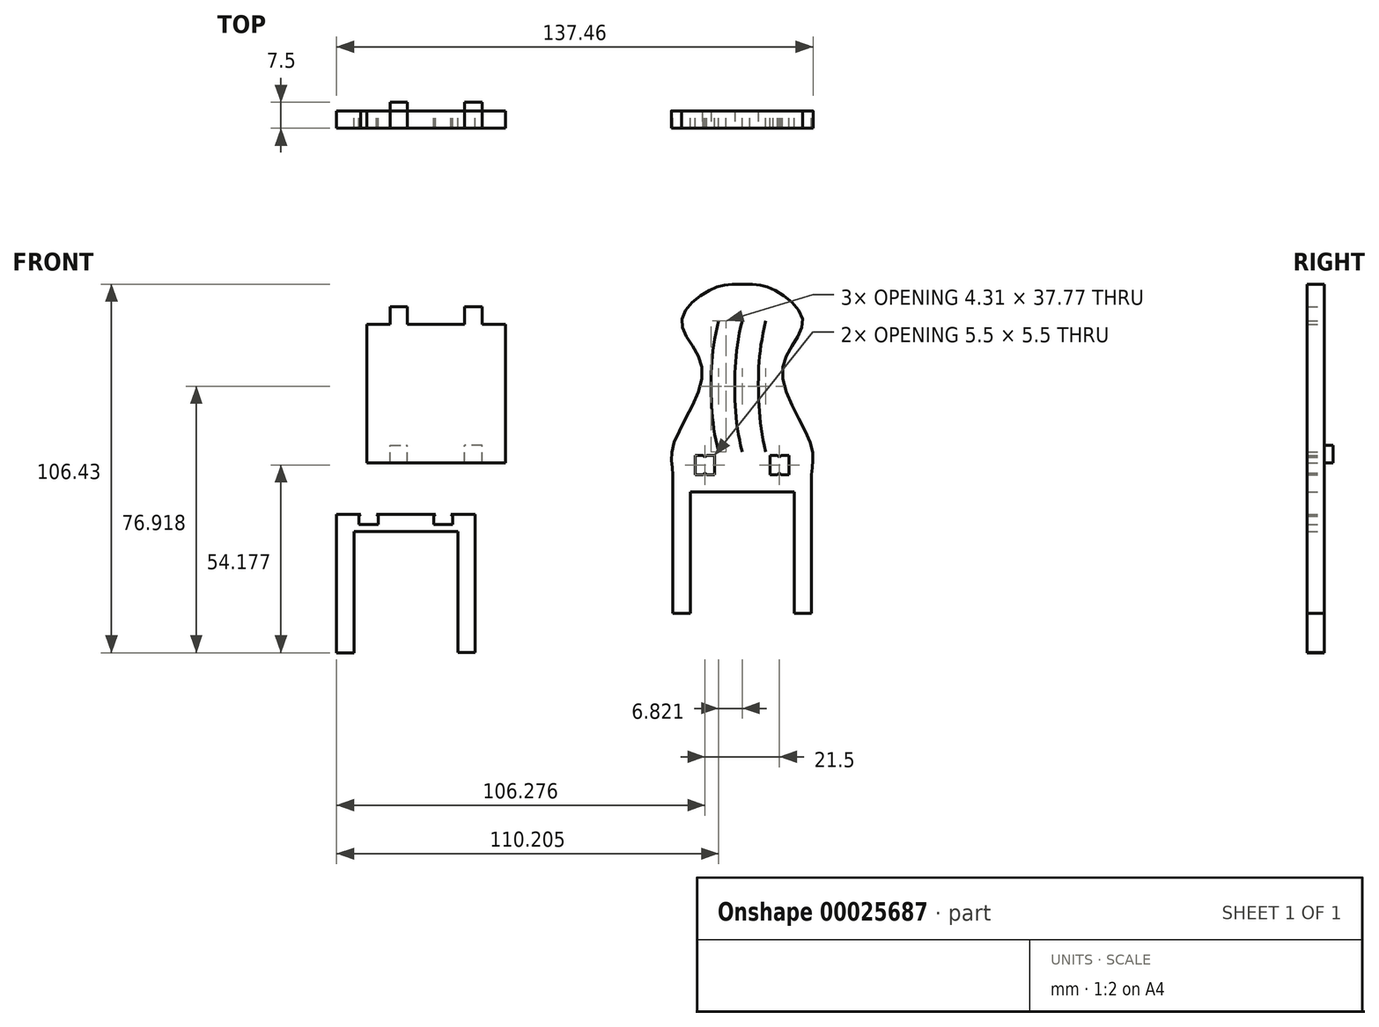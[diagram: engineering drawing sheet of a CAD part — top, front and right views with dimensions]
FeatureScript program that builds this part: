
annotation { "Feature Type Name" : "Feature", "Feature Type Description" : "" }
export const myFeature = defineFeature(function(context is Context, id is Id, definition is map)
    precondition{}
    {
        {
            var Q0;
            Q0=qCreatedBy(makeId("Front.planeOp"),FACE);
            var sketch = newSketch(context, id + "F0", { "sketchPlane" : qUnion([Q0])});
            skLineSegment(sketch, "E0.bottom", {"start": v(49.04, 57.77) * mm, "end": v(89.04, 57.77) * mm, "construction": true});
            skLineSegment(sketch, "E0.top", {"start": v(49.04, -37.23) * mm, "end": v(89.04, -37.23) * mm, "construction": true});
            skLineSegment(sketch, "E0.left", {"start": v(49.04, 57.77) * mm, "end": v(49.04, -37.23) * mm, "construction": true});
            skLineSegment(sketch, "E0.right", {"start": v(89.04, 57.77) * mm, "end": v(89.04, -37.23) * mm, "construction": true});
            skLineSegment(sketch, "E1", {"start": v(49.04, 2.77) * mm, "end": v(89.04, 2.77) * mm, "construction": true});
            skLineSegment(sketch, "E2", {"start": v(49.04, 2.77) * mm, "end": v(49.04, -37.23) * mm});
            skLineSegment(sketch, "E3", {"start": v(54.04, -37.23) * mm, "end": v(54.04, -2.23) * mm});
            skLineSegment(sketch, "E4", {"start": v(54.04, -2.23) * mm, "end": v(84.04, -2.23) * mm});
            skLineSegment(sketch, "E5", {"start": v(84.04, -2.23) * mm, "end": v(84.04, -37.23) * mm});
            skLineSegment(sketch, "E6", {"start": v(84.04, -37.23) * mm, "end": v(89.04, -37.23) * mm});
            skLineSegment(sketch, "E7", {"start": v(89.04, 2.77) * mm, "end": v(89.04, -37.23) * mm});
            skLineSegment(sketch, "E8", {"start": v(49.04, -37.23) * mm, "end": v(54.04, -37.23) * mm});
            skLineSegment(sketch, "E9", {"start": v(69.04, 57.77) * mm, "end": v(69.04, -0.66) * mm, "construction": true});
            skFitSpline(sketch, "E10", {"points": [v(49.04, 2.77) * mm, v(49.04, 10.95) * mm, v(57.45, 33.14) * mm, v(51.55, 46.97) * mm, v(59.84, 56.13) * mm, v(69.04, 57.77) * mm], "startDerivative": vector(0, 46.52) * mm, "endDerivative": vector(75.86, 0) * mm});
            skFitSpline(sketch, "E11.MirrorCS", {"points": [v(89.04, 2.77) * mm, v(89.04, 10.95) * mm, v(80.62, 33.14) * mm, v(86.52, 46.97) * mm, v(78.24, 56.13) * mm, v(69.04, 57.77) * mm], "startDerivative": vector(0, 46.52) * mm, "endDerivative": vector(-75.86, 0) * mm});
            skLineSegment(sketch, "E12", {"start": v(62.22, 47.14) * mm, "end": v(62.22, 9.37) * mm, "construction": true});
            skFitSpline(sketch, "E13", {"points": [v(62.22, 47.14) * mm, v(64.37, 28.26) * mm, v(62.22, 9.37) * mm], "startDerivative": vector(10.8, -41.93) * mm, "endDerivative": vector(-10.24, -39.43) * mm});
            skLineSegment(sketch, "E14", {"start": v(64.37, 28.26) * mm, "end": v(62.22, 28.26) * mm, "construction": true});
            skFitSpline(sketch, "E15.MirrorCS", {"points": [v(62.22, 47.14) * mm, v(60.06, 28.26) * mm, v(62.22, 9.37) * mm], "startDerivative": vector(-10.8, -41.93) * mm, "endDerivative": vector(10.24, -39.43) * mm});
            skFitSpline(sketch, "E16.MirrorCS", {"points": [v(75.86, 47.14) * mm, v(73.7, 28.26) * mm, v(75.86, 9.37) * mm], "startDerivative": vector(-10.8, -41.93) * mm, "endDerivative": vector(10.24, -39.43) * mm});
            skFitSpline(sketch, "E17.MirrorCS", {"points": [v(75.86, 47.14) * mm, v(78, 28.26) * mm, v(75.86, 9.37) * mm], "startDerivative": vector(10.8, -41.93) * mm, "endDerivative": vector(-10.24, -39.43) * mm});
            skFitSpline(sketch, "E18", {"points": [v(69.04, 47.14) * mm, v(71.19, 28.26) * mm, v(69.04, 9.37) * mm], "startDerivative": vector(10.8, -41.93) * mm, "endDerivative": vector(-10.24, -39.43) * mm});
            skLineSegment(sketch, "E19", {"start": v(69.04, 47.14) * mm, "end": v(69.04, 9.37) * mm, "construction": true});
            skFitSpline(sketch, "E20.MirrorCS", {"points": [v(69.04, 47.14) * mm, v(66.88, 28.26) * mm, v(69.04, 9.37) * mm], "startDerivative": vector(-10.8, -41.93) * mm, "endDerivative": vector(10.24, -39.43) * mm});
            skLineSegment(sketch, "E21", {"start": v(71.19, 28.26) * mm, "end": v(69.04, 28.26) * mm, "construction": true});
            skLineSegment(sketch, "E22.top", {"start": v(49.04, 8.27) * mm, "end": v(89.04, 8.27) * mm, "construction": true});
            skLineSegment(sketch, "E22.left", {"start": v(49.04, 2.77) * mm, "end": v(49.04, 8.27) * mm, "construction": true});
            skLineSegment(sketch, "E22.right", {"start": v(89.04, 2.77) * mm, "end": v(89.04, 8.27) * mm, "construction": true});
            skLineSegment(sketch, "E23.bottom", {"start": v(55.54, 8.27) * mm, "end": v(61.04, 8.27) * mm});
            skLineSegment(sketch, "E23.top", {"start": v(55.54, 2.77) * mm, "end": v(61.04, 2.77) * mm});
            skLineSegment(sketch, "E23.left", {"start": v(55.54, 8.27) * mm, "end": v(55.54, 2.77) * mm});
            skLineSegment(sketch, "E23.right", {"start": v(61.04, 8.27) * mm, "end": v(61.04, 2.77) * mm});
            skLineSegment(sketch, "E24", {"start": v(57.79, 8.27) * mm, "end": v(58.29, 7.77) * mm});
            skLineSegment(sketch, "E25", {"start": v(58.29, 7.77) * mm, "end": v(58.79, 8.27) * mm});
            skLineSegment(sketch, "E26", {"start": v(58.29, 7.77) * mm, "end": v(58.29, 8.27) * mm, "construction": true});
            skLineSegment(sketch, "E27", {"start": v(55.54, 5.52) * mm, "end": v(61.04, 5.52) * mm, "construction": true});
            skLineSegment(sketch, "E28.MirrorCS", {"start": v(57.79, 2.77) * mm, "end": v(58.29, 3.27) * mm});
            skLineSegment(sketch, "E29.MirrorCS", {"start": v(58.29, 3.27) * mm, "end": v(58.79, 2.77) * mm});
            skLineSegment(sketch, "E30.MirrorCS", {"start": v(79.79, 7.77) * mm, "end": v(79.79, 8.27) * mm});
            skLineSegment(sketch, "E31.MirrorCS", {"start": v(79.79, 7.77) * mm, "end": v(79.29, 8.27) * mm});
            skLineSegment(sketch, "E32.MirrorCS", {"start": v(80.29, 8.27) * mm, "end": v(79.79, 7.77) * mm});
            skLineSegment(sketch, "E33.MirrorCS", {"start": v(80.29, 2.77) * mm, "end": v(79.79, 3.27) * mm});
            skLineSegment(sketch, "E34.MirrorCS", {"start": v(79.79, 3.27) * mm, "end": v(79.29, 2.77) * mm});
            skLineSegment(sketch, "E35.MirrorCS", {"start": v(77.04, 8.27) * mm, "end": v(77.04, 2.77) * mm});
            skLineSegment(sketch, "E36.MirrorCS", {"start": v(82.54, 8.27) * mm, "end": v(77.04, 8.27) * mm});
            skLineSegment(sketch, "E37.MirrorCS", {"start": v(82.54, 5.52) * mm, "end": v(77.04, 5.52) * mm, "construction": true});
            skLineSegment(sketch, "E38.MirrorCS", {"start": v(82.54, 2.77) * mm, "end": v(77.04, 2.77) * mm});
            skLineSegment(sketch, "E39.MirrorCS", {"start": v(82.54, 8.27) * mm, "end": v(82.54, 2.77) * mm});
            skSolve(sketch);
        }
        {
            var Q0;
            Q0=makeQuery(id+"F0.imprint","IMPRINT",FACE,{"disambiguationData":[TD([[makeQuery(id+"F0.imprint","IMPRINT",EDGE,{"derivedFrom":sQuery(id+"F0.wireOp",EDGE,"E2")}),1.0]])]});
            var Q1;
            {var subQ1=sQuery(id+"F0.wireOp",EDGE,"E24");Q1=makeQuery(id+"F0.imprint","IMPRINT",FACE,{"disambiguationData":[TD([[makeQuery(id+"F0.imprint","IMPRINT",EDGE,{"derivedFrom":subQ1}),1.0]])]});}
            var Q2;
            {var subQ1=sQuery(id+"F0.wireOp",EDGE,"E28.MirrorCS");Q2=makeQuery(id+"F0.imprint","IMPRINT",FACE,{"disambiguationData":[TD([[makeQuery(id+"F0.imprint","IMPRINT",EDGE,{"derivedFrom":subQ1}),-1.0]])]});}
            var Q3;
            {var subQ2=sQuery(id+"F0.wireOp",EDGE,"E33.MirrorCS");Q3=makeQuery(id+"F0.imprint","IMPRINT",FACE,{"disambiguationData":[TD([[makeQuery(id+"F0.imprint","IMPRINT",EDGE,{"derivedFrom":subQ2}),1.0]])]});}
            var Q4;
            {var subQ2=sQuery(id+"F0.wireOp",EDGE,"E30.MirrorCS");Q4=makeQuery(id+"F0.imprint","IMPRINT",FACE,{"disambiguationData":[TD([[makeQuery(id+"F0.imprint","IMPRINT",EDGE,{"derivedFrom":subQ2}),1.0]])]});}
            var Q5;
            {var subQ2=sQuery(id+"F0.wireOp",EDGE,"E30.MirrorCS");Q5=makeQuery(id+"F0.imprint","IMPRINT",FACE,{"disambiguationData":[TD([[makeQuery(id+"F0.imprint","IMPRINT",EDGE,{"derivedFrom":subQ2}),-1.0]])]});}
            extrude(context, id + "F1", {"entities" : qUnion([Q0, Q1, Q2, Q3, Q4, Q5]), "depth" : 5 * mm});
        }
        {
            var Q0;
            Q0=qCreatedBy(makeId("Front.planeOp"),FACE);
            var sketch = newSketch(context, id + "F2", { "sketchPlane" : qUnion([Q0])});
            skLineSegment(sketch, "E40.bottom", {"start": v(-39.28, 46.22) * mm, "end": v(0.72, 46.22) * mm});
            skLineSegment(sketch, "E40.top", {"start": v(-39.28, 6.22) * mm, "end": v(0.72, 6.22) * mm});
            skLineSegment(sketch, "E40.left", {"start": v(-39.28, 46.22) * mm, "end": v(-39.28, 6.22) * mm});
            skLineSegment(sketch, "E40.right", {"start": v(0.72, 46.22) * mm, "end": v(0.72, 6.22) * mm});
            skLineSegment(sketch, "E41.bottom", {"start": v(-32.53, 46.22) * mm, "end": v(-27.53, 46.22) * mm});
            skLineSegment(sketch, "E41.top", {"start": v(-32.53, 51.22) * mm, "end": v(-27.53, 51.22) * mm});
            skLineSegment(sketch, "E41.left", {"start": v(-32.53, 46.22) * mm, "end": v(-32.53, 51.22) * mm});
            skLineSegment(sketch, "E41.right", {"start": v(-27.53, 46.22) * mm, "end": v(-27.53, 51.22) * mm});
            skLineSegment(sketch, "E42", {"start": v(-19.28, 46.22) * mm, "end": v(-19.28, 55.96) * mm, "construction": true});
            skLineSegment(sketch, "E43.MirrorCS", {"start": v(-6.03, 46.22) * mm, "end": v(-6.03, 51.22) * mm});
            skLineSegment(sketch, "E44.MirrorCS", {"start": v(-6.03, 51.22) * mm, "end": v(-11.03, 51.22) * mm});
            skLineSegment(sketch, "E45.MirrorCS", {"start": v(-6.03, 46.22) * mm, "end": v(-11.03, 46.22) * mm});
            skLineSegment(sketch, "E46.MirrorCS", {"start": v(0.72, 46.22) * mm, "end": v(-39.28, 46.22) * mm});
            skLineSegment(sketch, "E47.MirrorCS", {"start": v(-11.03, 46.22) * mm, "end": v(-11.03, 51.22) * mm});
            skSolve(sketch);
        }
        {
            var Q0;
            Q0=qSketchRegion(id+"F2",true);
            extrude(context, id + "F3", {"entities" : qUnion([Q0]), "depth" : 5 * mm});
        }
        {
            var Q0;
            Q0=qCreatedBy(makeId("Front.planeOp"),FACE);
            var sketch = newSketch(context, id + "F4", { "sketchPlane" : qUnion([Q0])});
            skLineSegment(sketch, "E48", {"start": v(-48, -8.66) * mm, "end": v(-48, -48.66) * mm});
            skLineSegment(sketch, "E49", {"start": v(-48, -48.66) * mm, "end": v(-43, -48.66) * mm});
            skLineSegment(sketch, "E50", {"start": v(-43, -48.66) * mm, "end": v(-43, -13.66) * mm});
            skLineSegment(sketch, "E51", {"start": v(-43, -13.66) * mm, "end": v(-13, -13.66) * mm});
            skLineSegment(sketch, "E52", {"start": v(-13, -13.66) * mm, "end": v(-13, -48.51) * mm});
            skLineSegment(sketch, "E53", {"start": v(-13, -48.51) * mm, "end": v(-8, -48.51) * mm});
            skLineSegment(sketch, "E54", {"start": v(-8, -48.51) * mm, "end": v(-8, -8.66) * mm});
            skLineSegment(sketch, "E55", {"start": v(-8, -8.66) * mm, "end": v(-48, -8.66) * mm});
            skSolve(sketch);
        }
        {
            var Q0;
            Q0=makeQuery(id+"F4.imprint","IMPRINT",FACE,{"disambiguationData":[TD([[makeQuery(id+"F4.imprint","IMPRINT",EDGE,{"derivedFrom":sQuery(id+"F4.wireOp",EDGE,"E48")}),1.0]])]});
            extrude(context, id + "F5", {"entities" : qUnion([Q0]), "depth" : 5 * mm});
        }
        {
            var Q0;
            Q0=makeQuery(id+"F3.opExtrude","CAP_FACE",FACE,{"disambiguationData":[OSD([sQuery(id+"F2.wireOp",EDGE,"E40.top"),sQuery(id+"F2.wireOp",EDGE,"E40.left"),sQuery(id+"F2.wireOp",EDGE,"E40.right"),sQuery(id+"F2.wireOp",EDGE,"E41.top"),sQuery(id+"F2.wireOp",EDGE,"E41.left"),sQuery(id+"F2.wireOp",EDGE,"E41.right"),sQuery(id+"F2.wireOp",EDGE,"E43.MirrorCS"),sQuery(id+"F2.wireOp",EDGE,"E44.MirrorCS"),sQuery(id+"F2.wireOp",EDGE,"E46.MirrorCS"),sQuery(id+"F2.wireOp",EDGE,"E47.MirrorCS")])],"isStart":true});
            var sketch = newSketch(context, id + "F6", { "sketchPlane" : qUnion([Q0])});
            skLineSegment(sketch, "E56.bottom", {"start": v(32.53, 6.22) * mm, "end": v(27.53, 6.22) * mm});
            skLineSegment(sketch, "E56.top", {"start": v(32.53, 11.22) * mm, "end": v(27.53, 11.22) * mm});
            skLineSegment(sketch, "E56.left", {"start": v(32.53, 6.22) * mm, "end": v(32.53, 11.22) * mm});
            skLineSegment(sketch, "E56.right", {"start": v(27.53, 6.22) * mm, "end": v(27.53, 11.22) * mm});
            skLineSegment(sketch, "E57", {"start": v(19.28, 6.22) * mm, "end": v(19.28, 17.56) * mm, "construction": true});
            skLineSegment(sketch, "E58.MirrorCS", {"start": v(6.03, 6.22) * mm, "end": v(11.03, 6.22) * mm});
            skLineSegment(sketch, "E59.MirrorCS", {"start": v(6.03, 11.22) * mm, "end": v(11.03, 11.22) * mm});
            skLineSegment(sketch, "E60.MirrorCS", {"start": v(6.03, 6.22) * mm, "end": v(6.03, 11.22) * mm});
            skLineSegment(sketch, "E61.MirrorCS", {"start": v(11.03, 6.22) * mm, "end": v(11.03, 11.22) * mm});
            skSolve(sketch);
        }
        {
            var Q0;
            Q0=makeQuery(id+"F6.imprint","IMPRINT",FACE,{"disambiguationData":[TD([[makeQuery(id+"F6.imprint","IMPRINT",EDGE,{"derivedFrom":sQuery(id+"F6.wireOp",EDGE,"E56.bottom")}),-1.0]])]});
            var Q1;
            Q1=makeQuery(id+"F6.imprint","IMPRINT",FACE,{"disambiguationData":[TD([[makeQuery(id+"F6.imprint","IMPRINT",EDGE,{"derivedFrom":sQuery(id+"F6.wireOp",EDGE,"E58.MirrorCS")}),-1.0]])]});
            extrude(context, id + "F7", {"entities" : qUnion([Q0, Q1]), "operationType" : NewBodyOperationType.ADD, "depth" : 2.5 * mm});
        }
        {
            var Q0;
            Q0=makeQuery(id+"F5.opExtrude","CAP_FACE",FACE,{"disambiguationData":[OSD([sQuery(id+"F4.wireOp",EDGE,"E48"),sQuery(id+"F4.wireOp",EDGE,"E49"),sQuery(id+"F4.wireOp",EDGE,"E50"),sQuery(id+"F4.wireOp",EDGE,"E51"),sQuery(id+"F4.wireOp",EDGE,"E52"),sQuery(id+"F4.wireOp",EDGE,"E53"),sQuery(id+"F4.wireOp",EDGE,"E54"),sQuery(id+"F4.wireOp",EDGE,"E55")])],"isStart":true});
            var sketch = newSketch(context, id + "F8", { "sketchPlane" : qUnion([Q0])});
            skLineSegment(sketch, "E62", {"start": v(28, -8.66) * mm, "end": v(28, -13.66) * mm, "construction": true});
            skLineSegment(sketch, "E63.bottom", {"start": v(14.5, -8.66) * mm, "end": v(20, -8.66) * mm});
            skLineSegment(sketch, "E63.top", {"start": v(14.5, -11.66) * mm, "end": v(20, -11.66) * mm});
            skLineSegment(sketch, "E63.left", {"start": v(14.5, -8.66) * mm, "end": v(14.5, -11.66) * mm});
            skLineSegment(sketch, "E63.right", {"start": v(20, -8.66) * mm, "end": v(20, -11.66) * mm});
            skLineSegment(sketch, "E64", {"start": v(14.5, -9.16) * mm, "end": v(15, -8.66) * mm});
            skLineSegment(sketch, "E65", {"start": v(17.24, -8.66) * mm, "end": v(17.24, -11.66) * mm, "construction": true});
            skLineSegment(sketch, "E66.MirrorCS", {"start": v(20, -9.16) * mm, "end": v(19.5, -8.66) * mm});
            skLineSegment(sketch, "E67.MirrorCS", {"start": v(20, -8.66) * mm, "end": v(14.5, -8.66) * mm});
            skLineSegment(sketch, "E68.MirrorCS", {"start": v(36, -9.16) * mm, "end": v(36.5, -8.66) * mm});
            skLineSegment(sketch, "E69.MirrorCS", {"start": v(41.5, -9.16) * mm, "end": v(41, -8.66) * mm});
            skLineSegment(sketch, "E70.MirrorCS", {"start": v(36, -8.66) * mm, "end": v(36, -11.66) * mm});
            skLineSegment(sketch, "E71.MirrorCS", {"start": v(41.5, -8.66) * mm, "end": v(36, -8.66) * mm});
            skLineSegment(sketch, "E72.MirrorCS", {"start": v(38.74, -8.66) * mm, "end": v(38.74, -11.66) * mm, "construction": true});
            skLineSegment(sketch, "E73.MirrorCS", {"start": v(41.5, -8.66) * mm, "end": v(41.5, -11.66) * mm});
            skLineSegment(sketch, "E74.MirrorCS", {"start": v(41.5, -11.66) * mm, "end": v(36, -11.66) * mm});
            skLineSegment(sketch, "E75.MirrorCS", {"start": v(36, -8.66) * mm, "end": v(41.5, -8.66) * mm});
            skSolve(sketch);
        }
        {
            var Q0;
            {var subQ4=sQuery(id+"F8.wireOp",EDGE,"E63.top");Q0=makeQuery(id+"F8.imprint","IMPRINT",FACE,{"disambiguationData":[TD([[makeQuery(id+"F8.imprint","IMPRINT",EDGE,{"derivedFrom":subQ4}),1.0]])]});}
            var Q1;
            {var subQ2=sQuery(id+"F8.wireOp",EDGE,"E68.MirrorCS");Q1=makeQuery(id+"F8.imprint","IMPRINT",FACE,{"disambiguationData":[TD([[makeQuery(id+"F8.imprint","IMPRINT",EDGE,{"derivedFrom":subQ2}),-1.0]])]});}
            extrude(context, id + "F9", {"entities" : qUnion([Q0, Q1]), "operationType" : NewBodyOperationType.REMOVE, "endBound" : BoundingType.THROUGH_ALL, "oppositeDirection" : true, "depth" : 25 * mm});
        }
    });
